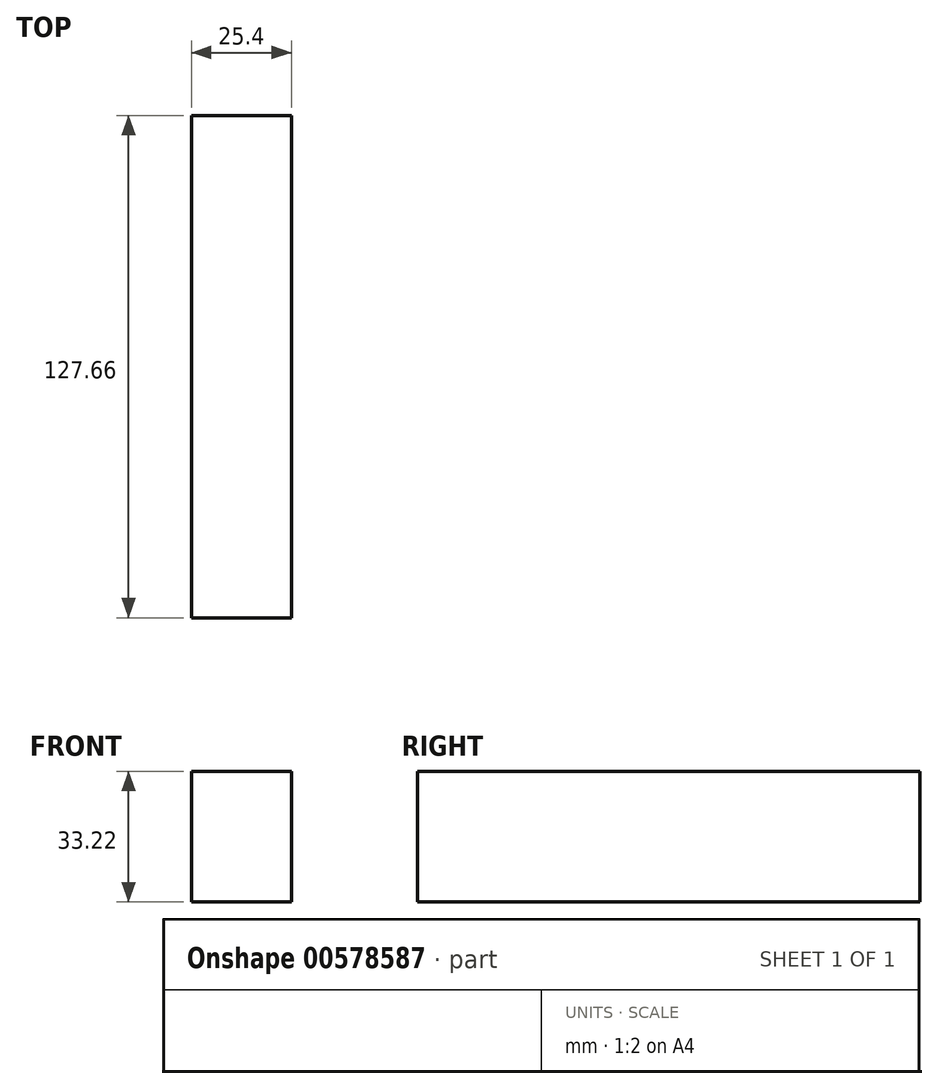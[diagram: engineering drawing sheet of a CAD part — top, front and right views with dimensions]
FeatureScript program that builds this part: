
annotation { "Feature Type Name" : "Feature", "Feature Type Description" : "" }
export const myFeature = defineFeature(function(context is Context, id is Id, definition is map)
    precondition{}
    {
        {
            var Q0;
            Q0=qCreatedBy(makeId("Right.planeOp"),FACE);
            var sketch = newSketch(context, id + "F0", { "sketchPlane" : qUnion([Q0])});
            skLineSegment(sketch, "E0.bottom", {"start": v(63.83, 16.6) * mm, "end": v(-63.83, 16.6) * mm});
            skLineSegment(sketch, "E0.top", {"start": v(63.83, -16.6) * mm, "end": v(-63.83, -16.6) * mm});
            skLineSegment(sketch, "E0.left", {"start": v(63.83, 16.6) * mm, "end": v(63.83, -16.6) * mm});
            skLineSegment(sketch, "E0.right", {"start": v(-63.83, 16.6) * mm, "end": v(-63.83, -16.6) * mm});
            skPoint(sketch, "E0.middle", {"position": v(0, 0) * mm});
            skSolve(sketch);
        }
        {
            var Q0;
            Q0=makeQuery(id+"F0.imprint","IMPRINT",FACE,{"disambiguationData":[TD([[makeQuery(id+"F0.imprint","IMPRINT",EDGE,{"derivedFrom":sQuery(id+"F0.wireOp",EDGE,"E0.bottom")}),1.0]])]});
            extrude(context, id + "F1", {"entities" : qUnion([Q0]), "depth" : 25.4 * mm, "offsetDistance" : 25.4 * mm});
        }
    });
